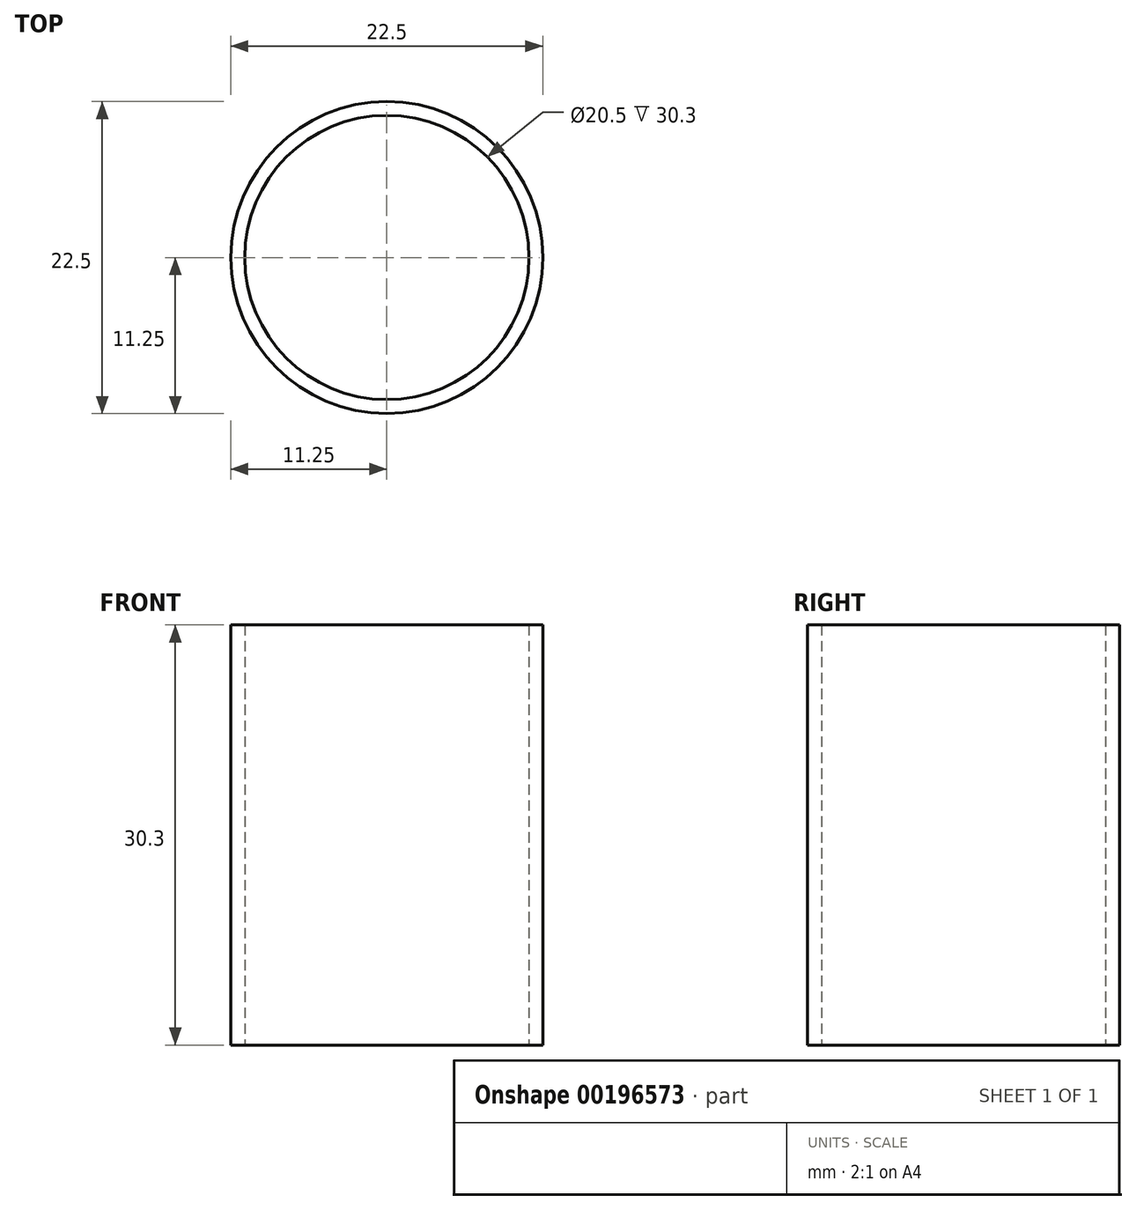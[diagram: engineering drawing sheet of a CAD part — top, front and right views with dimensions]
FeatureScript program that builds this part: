
annotation { "Feature Type Name" : "Feature", "Feature Type Description" : "" }
export const myFeature = defineFeature(function(context is Context, id is Id, definition is map)
    precondition{}
    {
        {
            var Q0;
            Q0=qCreatedBy(makeId("Front.planeOp"),FACE);
            var sketch = newSketch(context, id + "F0", { "sketchPlane" : qUnion([Q0])});
            skLineSegment(sketch, "E0", {"start": v(10.25, 0) * mm, "end": v(10.25, 30.3) * mm});
            skLineSegment(sketch, "E1", {"start": v(10.25, 30.3) * mm, "end": v(11.25, 30.3) * mm});
            skLineSegment(sketch, "E2", {"start": v(11.25, 30.3) * mm, "end": v(11.25, 0) * mm});
            skLineSegment(sketch, "E3", {"start": v(11.25, 0) * mm, "end": v(10.25, 0) * mm});
            skLineSegment(sketch, "E4", {"start": v(0, 0) * mm, "end": v(0, 30.3) * mm, "construction": true});
            skSolve(sketch);
        }
        {
            var Q0;
            Q0 = qSketchRegion(id + "F0", true);
            var Q1;
            Q1=sQuery(id+"F0.wireOp",EDGE,"E4");
            revolve(context, id + "F1", {"entities" : qUnion([Q0]), "axis" : qUnion([Q1]), "revolveType" : RevolveType.FULL});
        }
    });
